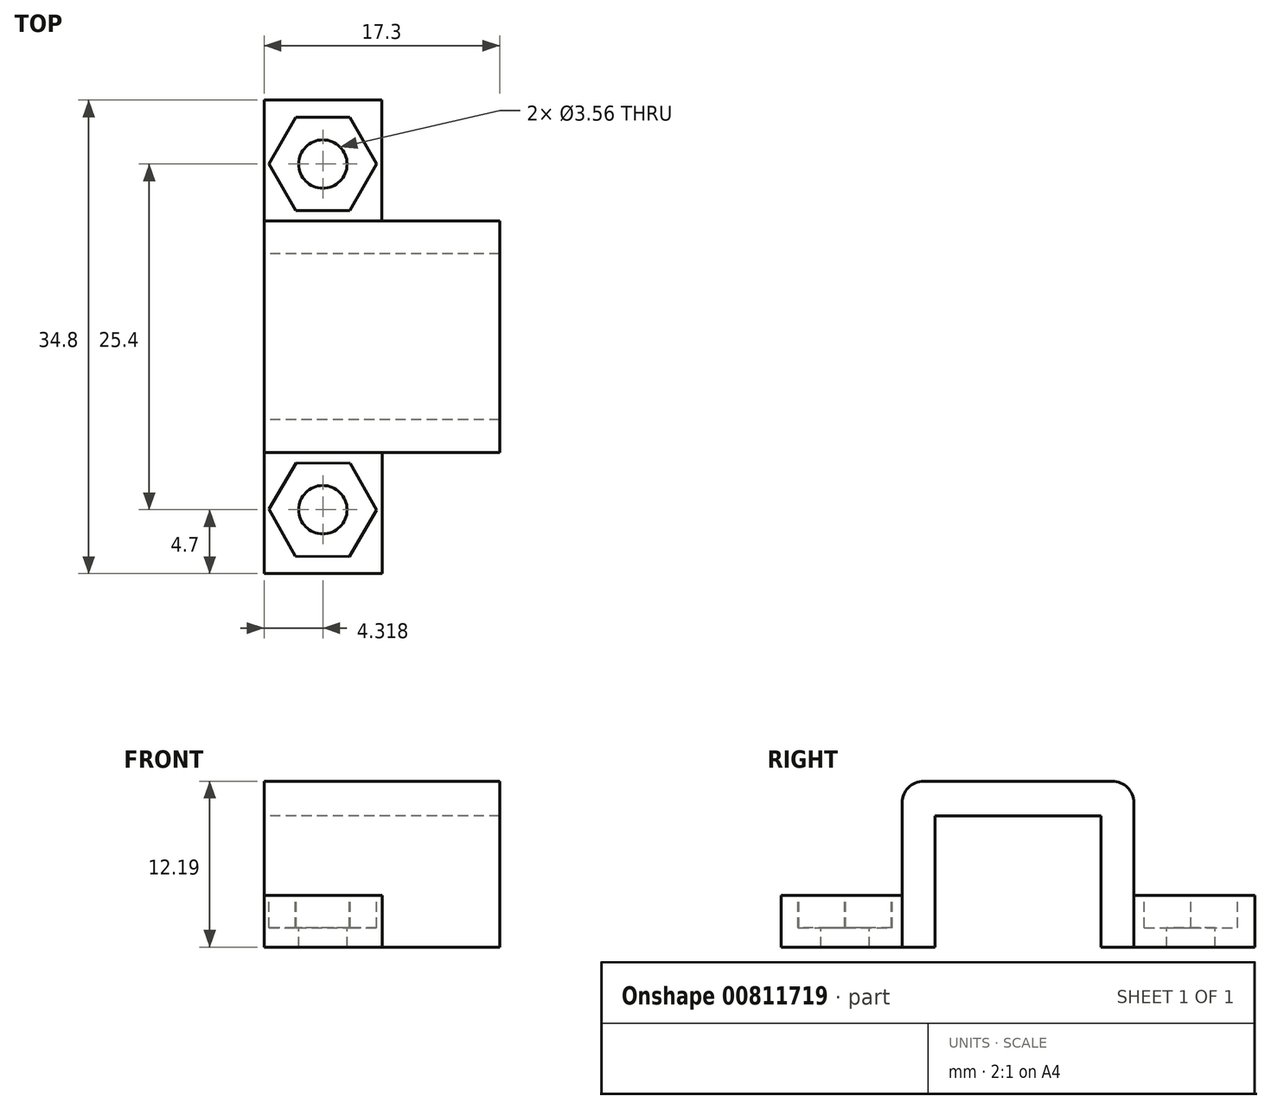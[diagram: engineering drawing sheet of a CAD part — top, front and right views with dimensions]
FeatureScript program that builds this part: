
annotation { "Feature Type Name" : "Feature", "Feature Type Description" : "" }
export const myFeature = defineFeature(function(context is Context, id is Id, definition is map)
    precondition{}
    {
        {
            var Q0;
            Q0=qCreatedBy(makeId("Right.planeOp"),FACE);
            var sketch = newSketch(context, id + "F0", { "sketchPlane" : qUnion([Q0])});
            skLineSegment(sketch, "E0", {"start": v(-17.4, 0) * mm, "end": v(-6.1, 0) * mm});
            skLineSegment(sketch, "E1", {"start": v(-6.1, 0) * mm, "end": v(-6.1, 9.65) * mm});
            skLineSegment(sketch, "E2", {"start": v(-6.1, 9.65) * mm, "end": v(0, 9.65) * mm});
            skLineSegment(sketch, "E3", {"start": v(-17.4, 0) * mm, "end": v(-17.4, 3.81) * mm});
            skLineSegment(sketch, "E4", {"start": v(-17.4, 3.81) * mm, "end": v(-8.5, 3.81) * mm});
            skLineSegment(sketch, "E5", {"start": v(-8.5, 3.81) * mm, "end": v(-8.5, 10.6) * mm});
            skLineSegment(sketch, "E6", {"start": v(-6.92, 12.2) * mm, "end": v(0, 12.2) * mm});
            skLineSegment(sketch, "E7", {"start": v(0, 12.2) * mm, "end": v(0, 9.65) * mm});
            skLineSegment(sketch, "E8", {"start": v(0, 12.2) * mm, "end": v(0, 0) * mm});
            skLineSegment(sketch, "E9.MirrorCS", {"start": v(17.4, 0) * mm, "end": v(17.4, 3.81) * mm});
            skLineSegment(sketch, "E10.MirrorCS", {"start": v(17.4, 3.81) * mm, "end": v(8.5, 3.81) * mm});
            skLineSegment(sketch, "E11.MirrorCS", {"start": v(17.4, 0) * mm, "end": v(6.1, 0) * mm});
            skLineSegment(sketch, "E12.MirrorCS", {"start": v(8.5, 3.81) * mm, "end": v(8.5, 10.6) * mm});
            skLineSegment(sketch, "E13.MirrorCS", {"start": v(6.1, 0) * mm, "end": v(6.1, 9.65) * mm});
            skLineSegment(sketch, "E14.MirrorCS", {"start": v(6.1, 9.65) * mm, "end": v(0, 9.65) * mm});
            skLineSegment(sketch, "E15.MirrorCS", {"start": v(6.92, 12.2) * mm, "end": v(0, 12.2) * mm});
            skPoint(sketch, "E16.visualSharp", {"position": v(-8.5, 12.2) * mm});
            skArc(sketch, "E16.filletArc", {"start": v(-6.92, 12.2) * mm, "mid": v(-8.04, 11.73) * mm, "end": v(-8.5, 10.6) * mm});
            skPoint(sketch, "E17.visualSharp", {"position": v(8.5, 12.2) * mm});
            skArc(sketch, "E17.filletArc", {"start": v(8.5, 10.6) * mm, "mid": v(8.04, 11.73) * mm, "end": v(6.92, 12.2) * mm});
            skSolve(sketch);
        }
        {
            var Q0;
            Q0 = qSketchRegion(id + "F0", true);
            var Q1;
            Q1=makeQuery(id+"F0.imprint","IMPRINT",FACE,{"disambiguationData":[TD([[makeQuery(id+"F0.imprint","IMPRINT",EDGE,{"derivedFrom":sQuery(id+"F0.wireOp",EDGE,"E0")}),1.0]])]});
            extrude(context, id + "F1", {"entities" : qUnion([Q0, Q1]), "depth" : 17.3 * mm, "offsetDistance" : 25.4 * mm});
        }
        {
            var Q0;
            Q0=makeQuery(id+"F1.opExtrude","SWEPT_FACE",FACE,{"disambiguationData":[OSD([sQuery(id+"F0.wireOp",EDGE,"E4")])]});
            var sketch = newSketch(context, id + "F2", { "sketchPlane" : qUnion([Q0])});
            skCircle(sketch, "E18", {"center": v(4.32, -12.7) * mm, "radius": 1.78 * mm});
            skLineSegment(sketch, "E19", {"start": v(0, -12.7) * mm, "end": v(4.32, -12.7) * mm});
            skCircle(sketch, "E20", {"center": v(4.32, -12.7) * mm, "radius": 3.43 * mm});
            skCircle(sketch, "E21.cCircle", {"center": v(4.32, -12.7) * mm, "radius": 3.43 * mm, "construction": true});
            skLineSegment(sketch, "E21.0", {"start": v(6.33, -9.29) * mm, "end": v(8.28, -12.73) * mm});
            skLineSegment(sketch, "E21.1", {"start": v(8.28, -12.73) * mm, "end": v(6.27, -16.15) * mm});
            skLineSegment(sketch, "E21.2", {"start": v(6.27, -16.15) * mm, "end": v(2.3, -16.11) * mm});
            skLineSegment(sketch, "E21.3", {"start": v(2.3, -16.11) * mm, "end": v(0.36, -12.67) * mm});
            skLineSegment(sketch, "E21.4", {"start": v(0.36, -12.67) * mm, "end": v(2.37, -9.25) * mm});
            skLineSegment(sketch, "E21.5", {"start": v(2.37, -9.25) * mm, "end": v(6.33, -9.29) * mm});
            skPoint(sketch, "E21.0.midPoint", {"position": v(7.3, -11.01) * mm});
            skLineSegment(sketch, "E22", {"start": v(4.32, -12.7) * mm, "end": v(4.32, 0) * mm});
            skSolve(sketch);
        }
        {
            var Q0;
            Q0=makeQuery(id+"F2.imprint","IMPRINT",FACE,{"disambiguationData":[TD([[makeQuery(id+"F2.imprint","IMPRINT",EDGE,{"derivedFrom":sQuery(id+"F2.wireOp",EDGE,"E18")}),1.0]])]});
            extrude(context, id + "F3", {"entities" : qUnion([Q0]), "operationType" : NewBodyOperationType.REMOVE, "oppositeDirection" : true, "depth" : 8.05 * mm, "offsetDistance" : 25.4 * mm});
        }
        {
            var Q0;
            Q0 = qSketchRegion(id + "F2", true);
            extrude(context, id + "F4", {"entities" : qUnion([Q0]), "operationType" : NewBodyOperationType.REMOVE, "oppositeDirection" : true, "depth" : 2.38 * mm, "offsetDistance" : 25.4 * mm});
        }
        {
            var Q0;
            Q0=makeQuery(id+"F1.opExtrude","SWEPT_FACE",FACE,{"disambiguationData":[OSD([sQuery(id+"F0.wireOp",EDGE,"E10.MirrorCS")])]});
            var sketch = newSketch(context, id + "F5", { "sketchPlane" : qUnion([Q0])});
            skCircle(sketch, "E23", {"center": v(4.32, 12.7) * mm, "radius": 1.78 * mm});
            skCircle(sketch, "E24", {"center": v(4.32, 12.7) * mm, "radius": 3.43 * mm});
            skCircle(sketch, "E25.cCircle", {"center": v(4.32, 12.7) * mm, "radius": 3.43 * mm, "construction": true});
            skPoint(sketch, "E25.0.midPoint", {"position": v(7.16, 14.62) * mm});
            skPoint(sketch, "E26.0.midPoint", {"position": v(6.27, 15.52) * mm});
            skLineSegment(sketch, "E27", {"start": v(4.32, 12.7) * mm, "end": v(4.32, 0) * mm});
            skLineSegment(sketch, "E28.0", {"start": v(2.34, 16.13) * mm, "end": v(6.3, 16.13) * mm});
            skLineSegment(sketch, "E28.1", {"start": v(6.3, 16.13) * mm, "end": v(8.28, 12.7) * mm});
            skLineSegment(sketch, "E28.2", {"start": v(8.28, 12.7) * mm, "end": v(6.3, 9.27) * mm});
            skLineSegment(sketch, "E28.3", {"start": v(6.3, 9.27) * mm, "end": v(2.34, 9.27) * mm});
            skLineSegment(sketch, "E28.4", {"start": v(2.34, 9.27) * mm, "end": v(0.36, 12.7) * mm});
            skLineSegment(sketch, "E28.5", {"start": v(0.36, 12.7) * mm, "end": v(2.34, 16.13) * mm});
            skPoint(sketch, "E28.0.midPoint", {"position": v(4.32, 16.13) * mm});
            skSolve(sketch);
        }
        {
            var Q0;
            Q0=makeQuery(id+"F5.imprint","IMPRINT",FACE,{"disambiguationData":[TD([[makeQuery(id+"F5.imprint","IMPRINT",EDGE,{"derivedFrom":sQuery(id+"F5.wireOp",EDGE,"E23")}),1.0]])]});
            extrude(context, id + "F6", {"entities" : qUnion([Q0]), "operationType" : NewBodyOperationType.REMOVE, "oppositeDirection" : true, "depth" : 13.97 * mm, "offsetDistance" : 25.4 * mm});
        }
        {
            var Q0;
            Q0 = qSketchRegion(id + "F5", true);
            extrude(context, id + "F7", {"entities" : qUnion([Q0]), "operationType" : NewBodyOperationType.REMOVE, "oppositeDirection" : true, "depth" : 2.38 * mm, "offsetDistance" : 25.4 * mm});
        }
        {
            var Q0;
            Q0=makeQuery(id+"F1.opExtrude","SWEPT_FACE",FACE,{"disambiguationData":[OSD([sQuery(id+"F0.wireOp",EDGE,"E10.MirrorCS")])]});
            var sketch = newSketch(context, id + "F8", { "sketchPlane" : qUnion([Q0])});
            skPoint(sketch, "E29.startSnap0", {"position": v(17.3, 12.95) * mm});
            skPoint(sketch, "E29.startSnap1", {"position": v(7.47, 11.42) * mm});
            skLineSegment(sketch, "E30", {"start": v(8.64, 17.4) * mm, "end": v(8.64, 8.5) * mm});
            skLineSegment(sketch, "E31", {"start": v(8.64, 8.5) * mm, "end": v(17.3, 8.5) * mm});
            skLineSegment(sketch, "E32", {"start": v(17.3, 8.5) * mm, "end": v(17.3, 17.4) * mm});
            skLineSegment(sketch, "E33", {"start": v(17.3, 17.4) * mm, "end": v(8.64, 17.4) * mm});
            skPoint(sketch, "E29.end.orphan", {"position": v(8.64, 12.7) * mm});
            skPoint(sketch, "E29.start.orphan", {"position": v(17.3, 11.42) * mm});
            skLineSegment(sketch, "E34", {"start": v(4.32, 16.13) * mm, "end": v(4.32, 9.27) * mm});
            skLineSegment(sketch, "E35", {"start": v(4.32, 12.7) * mm, "end": v(8.64, 12.7) * mm});
            skSolve(sketch);
        }
        {
            var Q0;
            Q0 = qSketchRegion(id + "F8", true);
            extrude(context, id + "F9", {"entities" : qUnion([Q0]), "operationType" : NewBodyOperationType.REMOVE, "oppositeDirection" : true, "depth" : 25.4 * mm, "offsetDistance" : 25.4 * mm});
        }
        {
            var Q0;
            Q0=makeQuery(id+"F1.opExtrude","SWEPT_FACE",FACE,{"disambiguationData":[OSD([sQuery(id+"F0.wireOp",EDGE,"E4")])]});
            var sketch = newSketch(context, id + "F10", { "sketchPlane" : qUnion([Q0])});
            skLineSegment(sketch, "E36", {"start": v(8.67, -8.5) * mm, "end": v(8.67, -17.4) * mm});
            skLineSegment(sketch, "E37", {"start": v(8.67, -17.4) * mm, "end": v(17.3, -17.4) * mm});
            skLineSegment(sketch, "E38", {"start": v(17.3, -17.4) * mm, "end": v(17.3, -8.5) * mm});
            skLineSegment(sketch, "E39", {"start": v(17.3, -8.5) * mm, "end": v(8.67, -8.5) * mm});
            skPoint(sketch, "E40.end.orphan", {"position": v(8.67, -12.95) * mm});
            skPoint(sketch, "E40.start.orphan", {"position": v(17.3, -12.95) * mm});
            skLineSegment(sketch, "E41", {"start": v(4.35, -12.67) * mm, "end": v(8.67, -12.67) * mm});
            skPoint(sketch, "E41.startSnap0", {"position": v(4.35, -9.27) * mm});
            skSolve(sketch);
        }
        {
            var Q0;
            Q0 = qSketchRegion(id + "F10", true);
            extrude(context, id + "F11", {"entities" : qUnion([Q0]), "operationType" : NewBodyOperationType.REMOVE, "oppositeDirection" : true, "depth" : 25.4 * mm, "offsetDistance" : 25.4 * mm});
        }
    });
